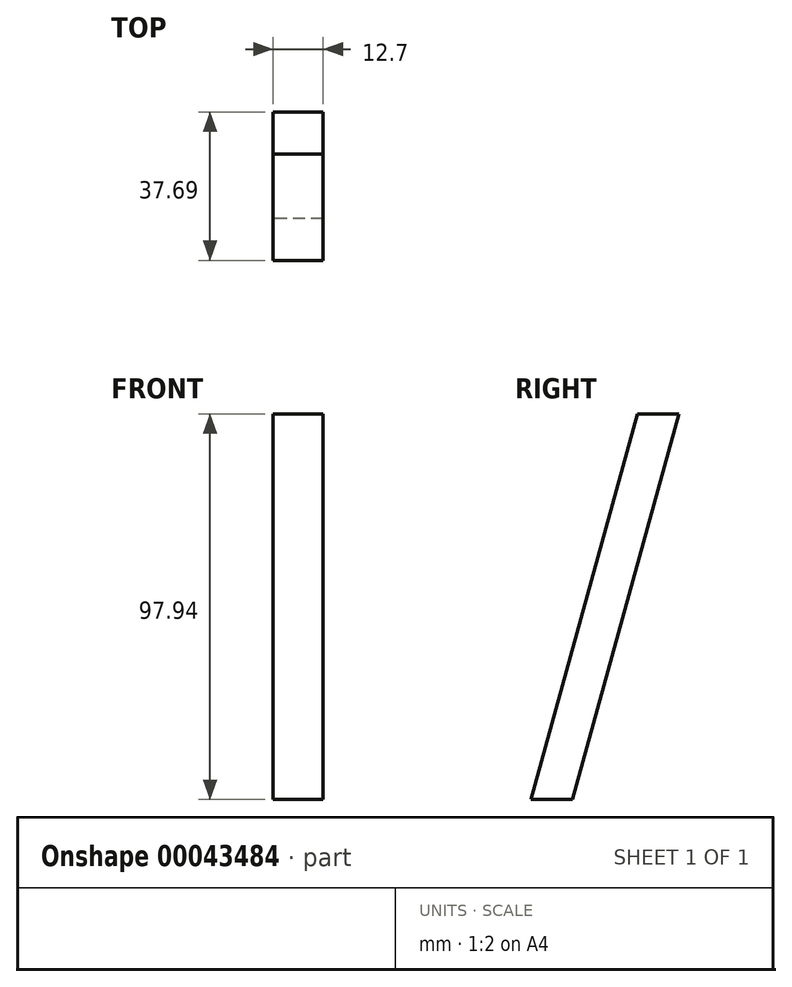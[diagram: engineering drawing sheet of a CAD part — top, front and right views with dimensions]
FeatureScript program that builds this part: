
annotation { "Feature Type Name" : "Feature", "Feature Type Description" : "" }
export const myFeature = defineFeature(function(context is Context, id is Id, definition is map)
    precondition{}
    {
        {
            var Q0;
            Q0=qCreatedBy(makeId("Right.planeOp"),FACE);
            var sketch = newSketch(context, id + "F0", { "sketchPlane" : qUnion([Q0])});
            skLineSegment(sketch, "E0", {"start": v(-8.86, 46.5) * mm, "end": v(1.78, 46.5) * mm});
            skLineSegment(sketch, "E1", {"start": v(1.78, 46.5) * mm, "end": v(-25.27, -51.43) * mm});
            skLineSegment(sketch, "E2", {"start": v(-25.27, -51.43) * mm, "end": v(-35.91, -51.43) * mm});
            skLineSegment(sketch, "E3", {"start": v(-35.91, -51.43) * mm, "end": v(-8.86, 46.5) * mm});
            skSolve(sketch);
        }
        {
            var Q0;
            Q0 = qSketchRegion(id + "F0", true);
            extrude(context, id + "F1", {"entities" : qUnion([Q0]), "depth" : 12.7 * mm});
        }
    });
